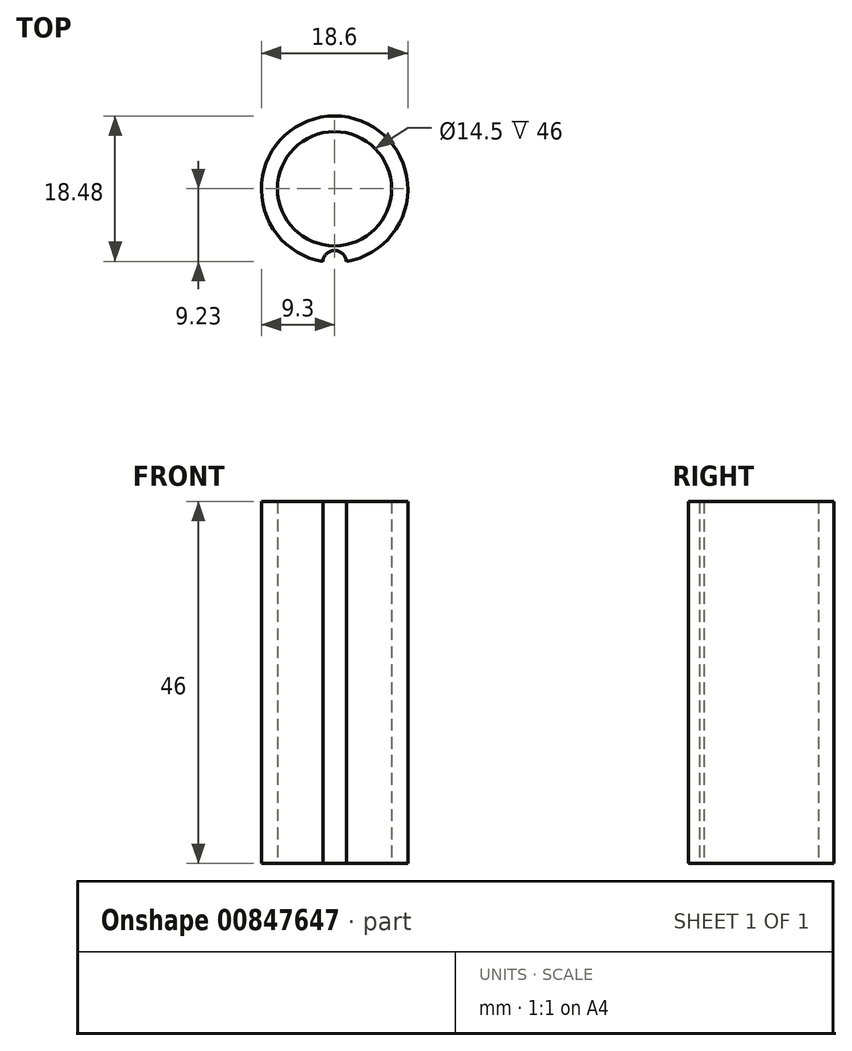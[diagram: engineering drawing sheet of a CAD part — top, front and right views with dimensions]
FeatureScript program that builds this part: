
annotation { "Feature Type Name" : "Feature", "Feature Type Description" : "" }
export const myFeature = defineFeature(function(context is Context, id is Id, definition is map)
    precondition{}
    {
        {
            var Q0;
            Q0=qCreatedBy(makeId("Top.planeOp"),FACE);
            var sketch = newSketch(context, id + "F0", { "sketchPlane" : qUnion([Q0])});
            skCircle(sketch, "E0", {"center": v(0, 0) * mm, "radius": 9.3 * mm});
            skCircle(sketch, "E1", {"center": v(0, 0.05) * mm, "radius": 7.25 * mm});
            skCircle(sketch, "E2", {"center": v(0, -9.3) * mm, "radius": 1.5 * mm});
            skSolve(sketch);
        }
        {
            var Q0;
            Q0=makeQuery(id+"F0.imprint","IMPRINT",FACE,{"disambiguationData":[TD([[makeQuery(id+"F0.imprint","IMPRINT",EDGE,{"derivedFrom":sQuery(id+"F0.wireOp",EDGE,"E1")}),-1.0]])]});
            extrude(context, id + "F1", {"entities" : qUnion([Q0]), "depth" : 46 * mm, "offsetDistance" : 25 * mm});
        }
    });
